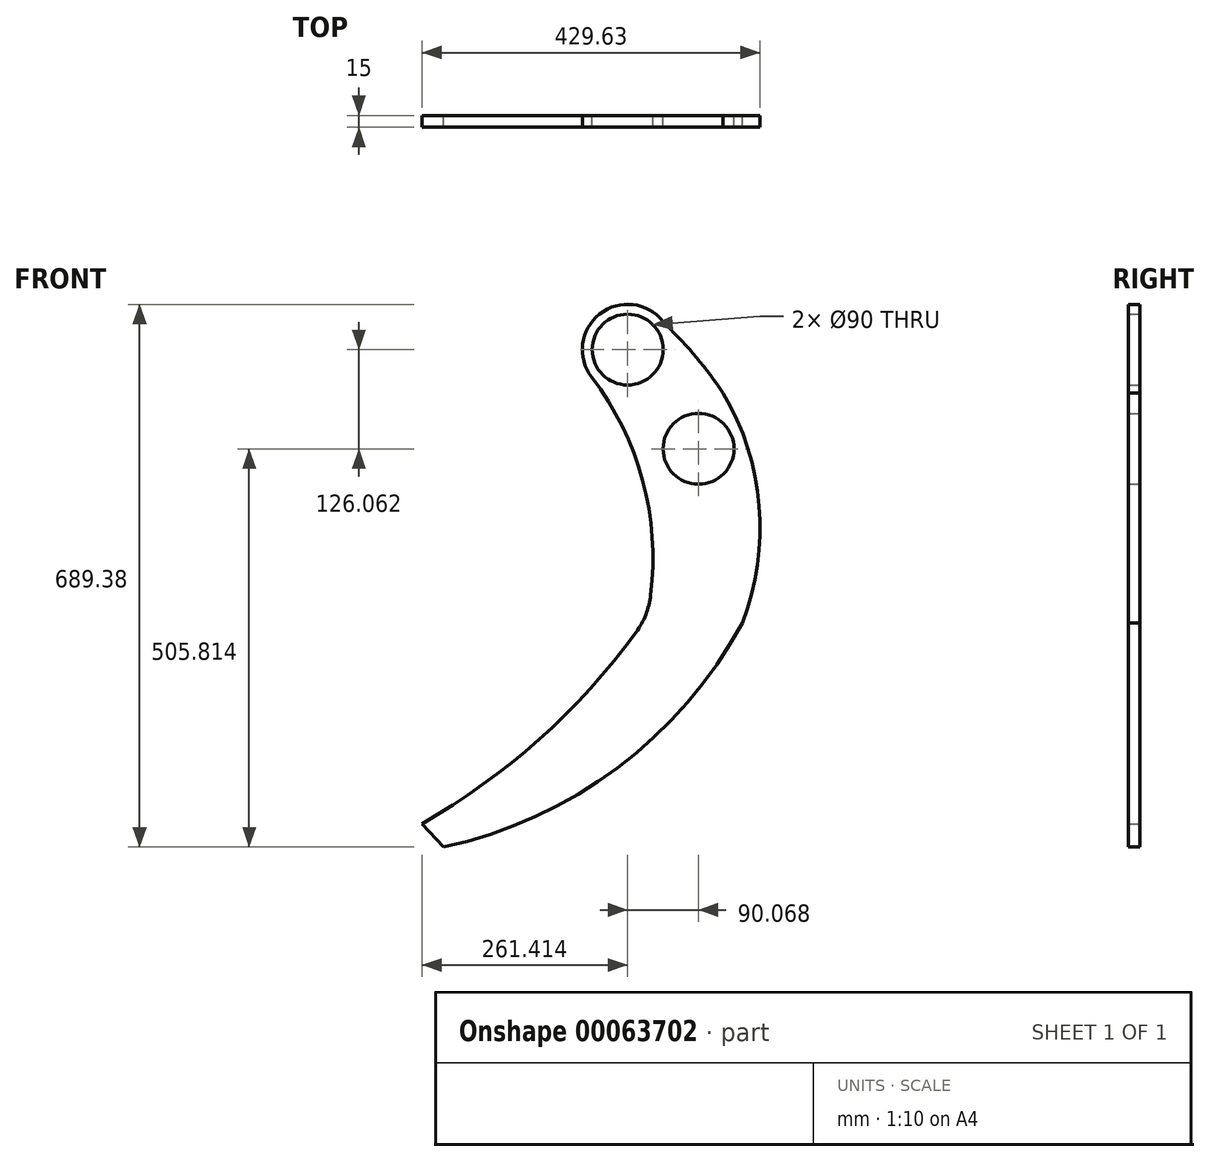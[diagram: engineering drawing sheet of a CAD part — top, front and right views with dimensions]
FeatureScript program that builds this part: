
annotation { "Feature Type Name" : "Feature", "Feature Type Description" : "" }
export const myFeature = defineFeature(function(context is Context, id is Id, definition is map)
    precondition{}
    {
        {
            var Q0;
            Q0=qCreatedBy(makeId("Front.planeOp"),FACE);
            var sketch = newSketch(context, id + "F0", { "sketchPlane" : qUnion([Q0])});
            skCircle(sketch, "E0", {"center": v(860.37, 943.57) * mm, "radius": 25 * mm});
            skArc(sketch, "E1", {"start": v(536.63, 437.76) * mm, "mid": v(757.51, 538.37) * mm, "end": v(915.87, 722.31) * mm});
            skArc(sketch, "E2", {"start": v(915.87, 722.31) * mm, "mid": v(937.38, 871.12) * mm, "end": v(891.67, 1014.37) * mm});
            skArc(sketch, "E3", {"start": v(891.67, 1014.37) * mm, "mid": v(857.82, 1059.5) * mm, "end": v(819.45, 1100.88) * mm});
            skLineSegment(sketch, "E4", {"start": v(508.89, 467.23) * mm, "end": v(536.63, 437.76) * mm});
            skArc(sketch, "E5", {"start": v(508.89, 467.23) * mm, "mid": v(657.77, 574.4) * mm, "end": v(780.97, 710.32) * mm});
            skCircle(sketch, "E6", {"center": v(770.3, 1069.64) * mm, "radius": 22.5 * mm});
            skCircle(sketch, "E7", {"center": v(770.3, 1069.64) * mm, "radius": 45 * mm});
            skCircle(sketch, "E8", {"center": v(860.37, 943.57) * mm, "radius": 45 * mm});
            skCircle(sketch, "E9", {"center": v(860.37, 943.57) * mm, "radius": 27.5 * mm});
            skArc(sketch, "E10", {"start": v(799.56, 757.71) * mm, "mid": v(789.44, 903.42) * mm, "end": v(724.85, 1034.42) * mm});
            skArc(sketch, "E11", {"start": v(780.97, 710.32) * mm, "mid": v(793.33, 732.81) * mm, "end": v(799.56, 757.71) * mm});
            skArc(sketch, "E12", {"start": v(815.22, 1105.53) * mm, "mid": v(734.75, 1114.82) * mm, "end": v(724.85, 1034.42) * mm});
            skArc(sketch, "E13", {"start": v(815.22, 1105.53) * mm, "mid": v(817.26, 1103.14) * mm, "end": v(819.45, 1100.88) * mm});
            skSolve(sketch);
        }
        {
            var Q0;
            Q0=makeQuery(id+"F0.imprint","IMPRINT",FACE,{"disambiguationData":[TD([[makeQuery(id+"F0.imprint","IMPRINT",EDGE,{"derivedFrom":sQuery(id+"F0.wireOp",EDGE,"E1")}),1.0]])]});
            extrude(context, id + "F1", {"entities" : qUnion([Q0]), "depth" : 15 * mm});
        }
    });
